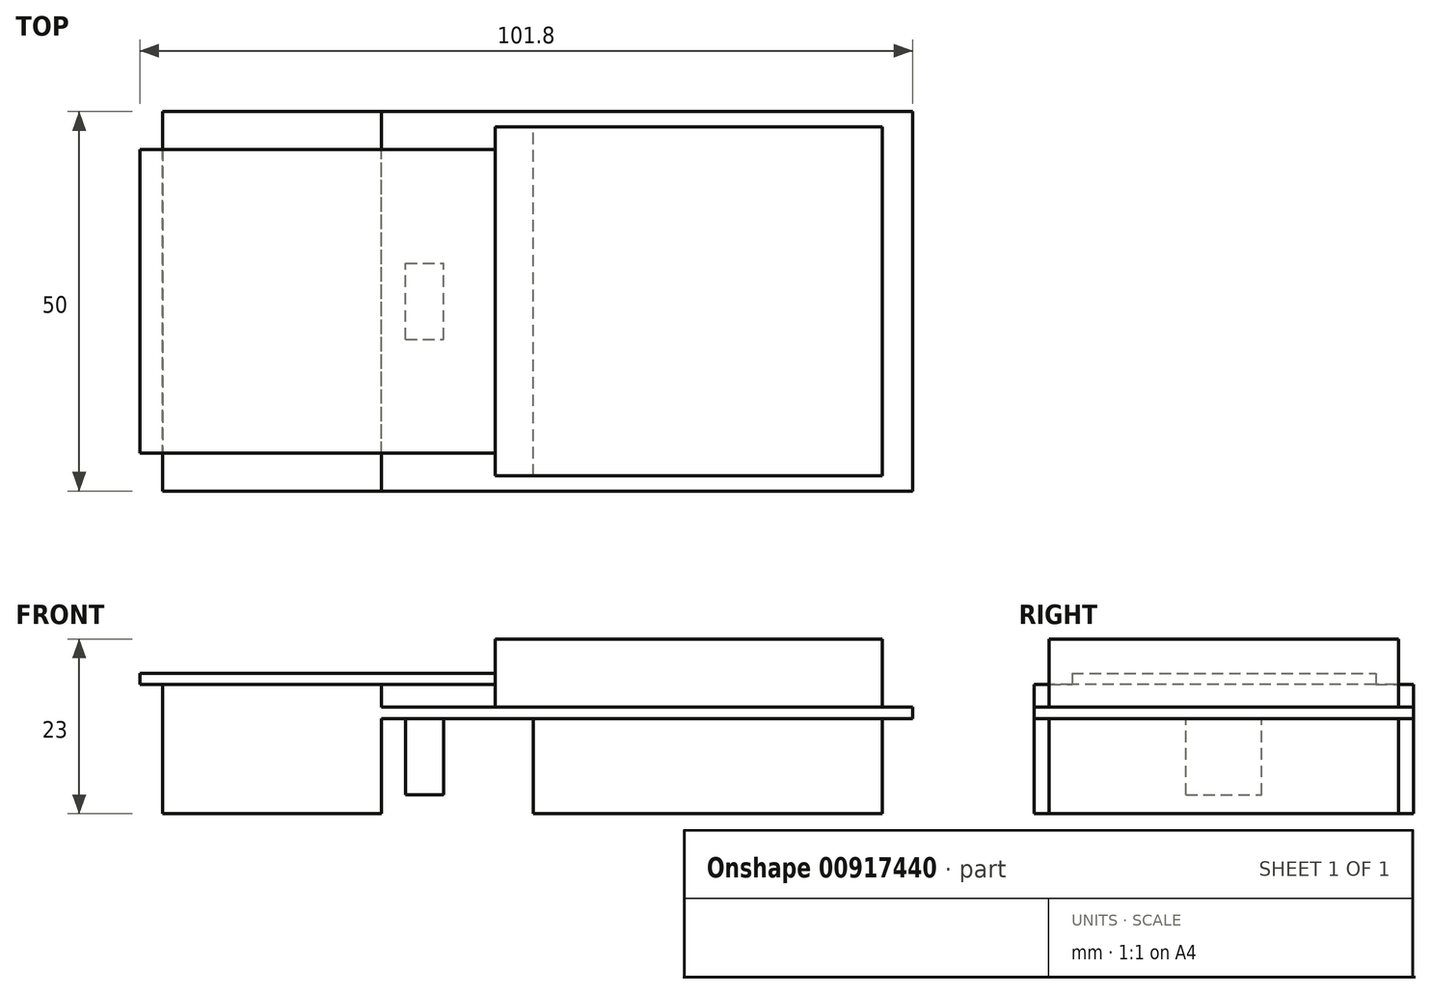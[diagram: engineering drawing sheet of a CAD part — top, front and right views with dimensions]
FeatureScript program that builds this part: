
annotation { "Feature Type Name" : "Feature", "Feature Type Description" : "" }
export const myFeature = defineFeature(function(context is Context, id is Id, definition is map)
    precondition{}
    {
        {
            var Q0;
            Q0=qCreatedBy(makeId("Top.planeOp"),FACE);
            var sketch = newSketch(context, id + "F0", { "sketchPlane" : qUnion([Q0])});
            skLineSegment(sketch, "E0.bottom", {"start": v(0, 0) * mm, "end": v(70, 0) * mm});
            skLineSegment(sketch, "E0.top", {"start": v(0, 50) * mm, "end": v(70, 50) * mm});
            skLineSegment(sketch, "E0.left", {"start": v(0, 0) * mm, "end": v(0, 50) * mm});
            skLineSegment(sketch, "E0.right", {"start": v(70, 0) * mm, "end": v(70, 50) * mm});
            skSolve(sketch);
        }
        {
            var Q0;
            Q0=makeQuery(id+"F0.imprint","IMPRINT",FACE,{"disambiguationData":[TD([[makeQuery(id+"F0.imprint","IMPRINT",EDGE,{"derivedFrom":sQuery(id+"F0.wireOp",EDGE,"E0.bottom")}),1.0]])]});
            extrude(context, id + "F1", {"entities" : qUnion([Q0]), "depth" : 1.5 * mm, "offsetDistance" : 25 * mm});
        }
        {
            var Q0;
            Q0=makeQuery(id+"F1.opExtrude","CAP_FACE",FACE,{"disambiguationData":[OSD([sQuery(id+"F0.wireOp",EDGE,"E0.bottom"),sQuery(id+"F0.wireOp",EDGE,"E0.top"),sQuery(id+"F0.wireOp",EDGE,"E0.left"),sQuery(id+"F0.wireOp",EDGE,"E0.right")])],"isStart":true});
            var sketch = newSketch(context, id + "F2", { "sketchPlane" : qUnion([Q0])});
            skLineSegment(sketch, "E1.bottom", {"start": v(66, -2) * mm, "end": v(20, -2) * mm});
            skLineSegment(sketch, "E1.top", {"start": v(66, -48) * mm, "end": v(20, -48) * mm});
            skLineSegment(sketch, "E1.left", {"start": v(66, -2) * mm, "end": v(66, -48) * mm});
            skLineSegment(sketch, "E1.right", {"start": v(20, -2) * mm, "end": v(20, -48) * mm});
            skLineSegment(sketch, "E2.bottom", {"start": v(3.2, -20) * mm, "end": v(8.2, -20) * mm});
            skLineSegment(sketch, "E2.top", {"start": v(3.2, -30) * mm, "end": v(8.2, -30) * mm});
            skLineSegment(sketch, "E2.left", {"start": v(3.2, -20) * mm, "end": v(3.2, -30) * mm});
            skLineSegment(sketch, "E2.right", {"start": v(8.2, -20) * mm, "end": v(8.2, -30) * mm});
            skSolve(sketch);
        }
        {
            var Q0;
            Q0=makeQuery(id+"F2.imprint","IMPRINT",FACE,{"disambiguationData":[TD([[makeQuery(id+"F2.imprint","IMPRINT",EDGE,{"derivedFrom":sQuery(id+"F2.wireOp",EDGE,"E1.bottom")}),1.0]])]});
            extrude(context, id + "F3", {"entities" : qUnion([Q0]), "operationType" : NewBodyOperationType.ADD, "depth" : 12.5 * mm, "offsetDistance" : 25 * mm});
        }
        {
            var Q0;
            Q0=makeQuery(id+"F2.imprint","IMPRINT",FACE,{"disambiguationData":[TD([[makeQuery(id+"F2.imprint","IMPRINT",EDGE,{"derivedFrom":sQuery(id+"F2.wireOp",EDGE,"E2.bottom")}),-1.0]])]});
            extrude(context, id + "F4", {"entities" : qUnion([Q0]), "operationType" : NewBodyOperationType.ADD, "depth" : 10 * mm, "offsetDistance" : 25 * mm});
        }
        {
            var Q0;
            Q0=makeQuery(id+"F1.opExtrude","CAP_FACE",FACE,{"disambiguationData":[OSD([sQuery(id+"F0.wireOp",EDGE,"E0.bottom"),sQuery(id+"F0.wireOp",EDGE,"E0.top"),sQuery(id+"F0.wireOp",EDGE,"E0.left"),sQuery(id+"F0.wireOp",EDGE,"E0.right")])],"isStart":false});
            var sketch = newSketch(context, id + "F5", { "sketchPlane" : qUnion([Q0])});
            skLineSegment(sketch, "E3.bottom", {"start": v(66, 48) * mm, "end": v(15, 48) * mm});
            skLineSegment(sketch, "E3.top", {"start": v(66, 2) * mm, "end": v(15, 2) * mm});
            skLineSegment(sketch, "E3.left", {"start": v(66, 48) * mm, "end": v(66, 2) * mm});
            skLineSegment(sketch, "E3.right", {"start": v(15, 48) * mm, "end": v(15, 2) * mm});
            skSolve(sketch);
        }
        {
            var Q0;
            Q0=makeQuery(id+"F5.imprint","IMPRINT",FACE,{"disambiguationData":[TD([[makeQuery(id+"F5.imprint","IMPRINT",EDGE,{"derivedFrom":sQuery(id+"F5.wireOp",EDGE,"E3.bottom")}),1.0]])]});
            extrude(context, id + "F6", {"entities" : qUnion([Q0]), "operationType" : NewBodyOperationType.ADD, "depth" : 9 * mm, "offsetDistance" : 25 * mm});
        }
        {
            var Q0;
            Q0=makeQuery(id+"F1.opExtrude","SWEPT_FACE",FACE,{"disambiguationData":[OSD([sQuery(id+"F0.wireOp",EDGE,"E0.left")])]});
            var sketch = newSketch(context, id + "F7", { "sketchPlane" : qUnion([Q0])});
            skLineSegment(sketch, "E4.bottom", {"start": v(0, 4.5) * mm, "end": v(-50, 4.5) * mm});
            skLineSegment(sketch, "E4.top", {"start": v(0, -12.5) * mm, "end": v(-50, -12.5) * mm});
            skLineSegment(sketch, "E4.left", {"start": v(0, 4.5) * mm, "end": v(0, -12.5) * mm});
            skLineSegment(sketch, "E4.right", {"start": v(-50, 4.5) * mm, "end": v(-50, -12.5) * mm});
            skSolve(sketch);
        }
        {
            var Q0;
            {var subQ0=sQuery(id+"F7.wireOp",EDGE,"E4.bottom");Q0=makeQuery(id+"F7.imprint","IMPRINT",FACE,{"disambiguationData":[TD([[makeQuery(id+"F7.imprint","IMPRINT",EDGE,{"derivedFrom":subQ0}),1.0]])]});}
            var Q1;
            {var subQ1=sQuery(id+"F0.wireOp",EDGE,"E0.left");var subQ2=makeQuery(id+"F1.opExtrude","CAP_EDGE",EDGE,{"disambiguationData":[OSD([subQ1])],"isStart":true});Q1=makeQuery(id+"F7.imprint","IMPRINT",FACE,{"disambiguationData":[TD([[makeQuery(id+"F7.imprint","IMPRINT",EDGE,{"derivedFrom":subQ2}),-1.0]])]});}
            var Q2;
            {var subQ0=sQuery(id+"F7.wireOp",EDGE,"E4.top");Q2=makeQuery(id+"F7.imprint","IMPRINT",FACE,{"disambiguationData":[TD([[makeQuery(id+"F7.imprint","IMPRINT",EDGE,{"derivedFrom":subQ0}),-1.0]])]});}
            extrude(context, id + "F8", {"entities" : qUnion([Q0, Q1, Q2]), "operationType" : NewBodyOperationType.ADD, "depth" : 31.8 * mm, "offsetDistance" : 25 * mm});
        }
        {
            var Q0;
            Q0=makeQuery(id+"F8.opExtrude","SWEPT_FACE",FACE,{"disambiguationData":[OSD([sQuery(id+"F7.wireOp",EDGE,"E4.bottom")])]});
            var sketch = newSketch(context, id + "F9", { "sketchPlane" : qUnion([Q0])});
            skLineSegment(sketch, "E5.bottom", {"start": v(-31.8, 45) * mm, "end": v(15, 45) * mm});
            skLineSegment(sketch, "E5.top", {"start": v(-31.8, 5) * mm, "end": v(15, 5) * mm});
            skLineSegment(sketch, "E5.left", {"start": v(-31.8, 45) * mm, "end": v(-31.8, 5) * mm});
            skLineSegment(sketch, "E5.right", {"start": v(15, 45) * mm, "end": v(15, 5) * mm});
            skSolve(sketch);
        }
        {
            var Q0;
            {var subQ0=sQuery(id+"F9.wireOp",EDGE,"E5.left");Q0=makeQuery(id+"F9.imprint","IMPRINT",FACE,{"disambiguationData":[TD([[makeQuery(id+"F9.imprint","IMPRINT",EDGE,{"derivedFrom":subQ0}),-1.0]])]});}
            var Q1;
            {var subQ0=sQuery(id+"F9.wireOp",EDGE,"E5.right");Q1=makeQuery(id+"F9.imprint","IMPRINT",FACE,{"disambiguationData":[TD([[makeQuery(id+"F9.imprint","IMPRINT",EDGE,{"derivedFrom":subQ0}),-1.0]])]});}
            extrude(context, id + "F10", {"entities" : qUnion([Q0, Q1]), "operationType" : NewBodyOperationType.ADD, "depth" : 1.5 * mm, "offsetDistance" : 25 * mm});
        }
        {
            var Q0;
            Q0=makeQuery(id+"F10.boolean.opBoolean","MERGE",FACE,{"derivedFrom":[makeQuery(id+"F8.opExtrude","CAP_FACE",FACE,{"disambiguationData":[OSD([sQuery(id+"F7.wireOp",EDGE,"E4.bottom"),sQuery(id+"F7.wireOp",EDGE,"E4.top"),sQuery(id+"F7.wireOp",EDGE,"E4.left"),sQuery(id+"F7.wireOp",EDGE,"E4.right")])],"isStart":false}),makeQuery(id+"F10.opExtrude","SWEPT_FACE",FACE,{"disambiguationData":[OSD([sQuery(id+"F9.wireOp",EDGE,"E5.left")])]})]});
            var sketch = newSketch(context, id + "F11", { "sketchPlane" : qUnion([Q0])});
            skLineSegment(sketch, "E6", {"start": v(-45, 4.5) * mm, "end": v(-5, 4.5) * mm});
            skSolve(sketch);
        }
        {
            var Q0;
            Q0 = qSketchRegion(id + "F11", true);
            var Q1;
            Q1=makeQuery(id+"F11.imprint","IMPRINT",FACE,{"disambiguationData":[TD([[makeQuery(id+"F11.imprint","IMPRINT",EDGE,{"derivedFrom":sQuery(id+"F11.wireOp",EDGE,"E6")}),-1.0]])]});
            extrude(context, id + "F12", {"entities" : qUnion([Q0, Q1]), "operationType" : NewBodyOperationType.REMOVE, "oppositeDirection" : true, "depth" : 3 * mm, "offsetDistance" : 25 * mm});
        }
    });
